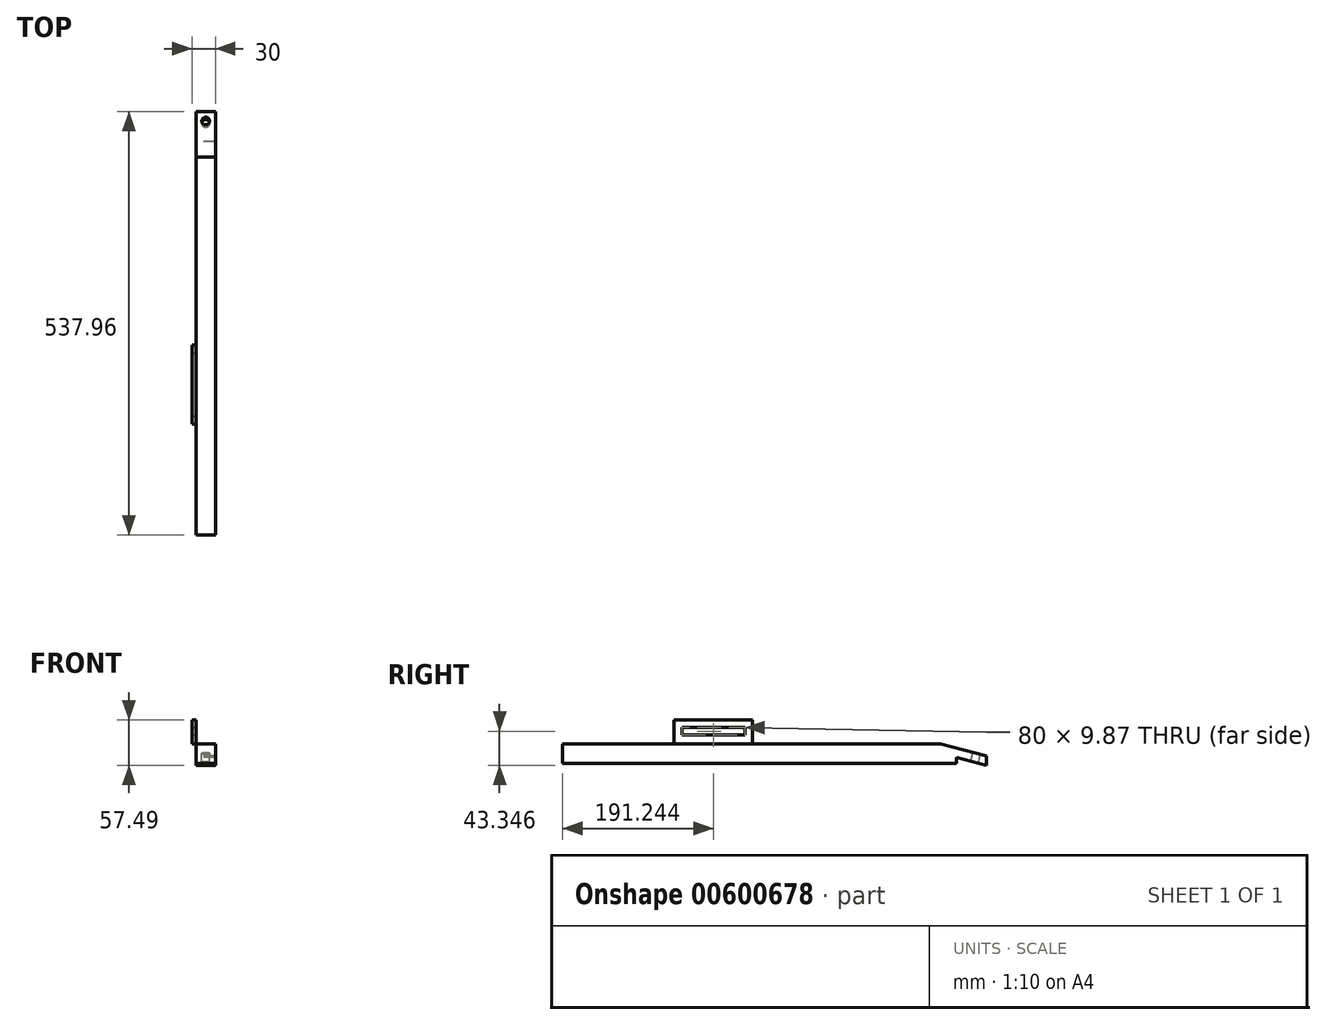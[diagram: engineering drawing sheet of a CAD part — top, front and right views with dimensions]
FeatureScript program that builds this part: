
annotation { "Feature Type Name" : "Feature", "Feature Type Description" : "" }
export const myFeature = defineFeature(function(context is Context, id is Id, definition is map)
    precondition{}
    {
        {
            var Q0;
            Q0=qCreatedBy(makeId("Right.planeOp"),FACE);
            var sketch = newSketch(context, id + "F0", { "sketchPlane" : qUnion([Q0])});
            skLineSegment(sketch, "E0.bottom", {"start": v(0, 0) * mm, "end": v(500, 0) * mm});
            skLineSegment(sketch, "E0.left", {"start": v(0, 0) * mm, "end": v(0, 25) * mm});
            skLineSegment(sketch, "E1", {"start": v(480, 25) * mm, "end": v(537.96, 9.47) * mm});
            skLineSegment(sketch, "E2", {"start": v(537.96, 9.47) * mm, "end": v(537.94, -2.49) * mm});
            skLineSegment(sketch, "E3", {"start": v(480, 25) * mm, "end": v(0, 25) * mm});
            skLineSegment(sketch, "E4", {"start": v(0, 25) * mm, "end": v(0, 0) * mm});
            skLineSegment(sketch, "E5", {"start": v(500, 0) * mm, "end": v(500, 7.68) * mm});
            skLineSegment(sketch, "E6", {"start": v(500, 7.68) * mm, "end": v(537.94, -2.49) * mm});
            skSolve(sketch);
        }
        {
            var Q0;
            Q0=makeQuery(id+"F0.imprint","IMPRINT",FACE,{"disambiguationData":[TD([[makeQuery(id+"F0.imprint","IMPRINT",EDGE,{"derivedFrom":sQuery(id+"F0.wireOp",EDGE,"E1")}),-1.0]])]});
            extrude(context, id + "F1", {"entities" : qUnion([Q0]), "depth" : 25 * mm, "offsetDistance" : 25 * mm});
        }
        {
            var Q0;
            Q0=makeQuery(id+"F1.opExtrude","SWEPT_FACE",FACE,{"disambiguationData":[OSD([sQuery(id+"F0.wireOp",EDGE,"E1")])]});
            var sketch = newSketch(context, id + "F2", { "sketchPlane" : qUnion([Q0])});
            skLineSegment(sketch, "E7.bottom", {"start": v(0, 517.17) * mm, "end": v(25, 517.17) * mm});
            skLineSegment(sketch, "E7.top", {"start": v(0, 457.17) * mm, "end": v(25, 457.17) * mm});
            skLineSegment(sketch, "E7.left", {"start": v(0, 517.17) * mm, "end": v(0, 457.17) * mm});
            skLineSegment(sketch, "E7.right", {"start": v(25, 517.17) * mm, "end": v(25, 457.17) * mm});
            skLineSegment(sketch, "E8", {"start": v(12.5, 517.17) * mm, "end": v(12.5, 504.83) * mm});
            skPoint(sketch, "E8.endSnap0", {"position": v(12.5, 517.17) * mm});
            skCircle(sketch, "E9", {"center": v(12.5, 504.83) * mm, "radius": 5 * mm});
            skSolve(sketch);
        }
        {
            var Q0;
            Q0=sQuery(id+"F2.wireOp",VERTEX,"E9.center");
            var Q1;
            Q1=makeQuery(id+"F1.opExtrude","SWEPT_BODY",BODY,{"disambiguationData":[OSD([sQuery(id+"F0.wireOp",EDGE,"E1"),sQuery(id+"F0.wireOp",EDGE,"E2"),sQuery(id+"F0.wireOp",EDGE,"E3"),sQuery(id+"F0.wireOp",EDGE,"E4"),sQuery(id+"F0.wireOp",EDGE,"E0.bottom"),sQuery(id+"F0.wireOp",EDGE,"E5"),sQuery(id+"F0.wireOp",EDGE,"E6")])]});
            hole(context, id + "F3", {"style" : HoleStyle.SIMPLE, "endStyle" : HoleEndStyle.THROUGH, "holeDiameter" : 10 * mm, "majorDiameter" : 5 * mm, "isTappedThrough" : true, "tappedDepth" : 12 * mm, "tapClearance" : 3, "locations" : qUnion([Q0]), "scope" : qUnion([Q1])});
        }
        {
            var Q0;
            Q0=makeQuery(id+"F0.imprint","IMPRINT",FACE,{"disambiguationData":[TD([[makeQuery(id+"F0.imprint","IMPRINT",EDGE,{"derivedFrom":sQuery(id+"F0.wireOp",EDGE,"E1")}),-1.0]])]});
            var sketch = newSketch(context, id + "F4", { "sketchPlane" : qUnion([Q0])});
            skLineSegment(sketch, "E10.bottom", {"start": v(0, 0) * mm, "end": v(482.49, 0) * mm});
            skLineSegment(sketch, "E10.top", {"start": v(0, 25.03) * mm, "end": v(482.49, 25.03) * mm});
            skLineSegment(sketch, "E10.left", {"start": v(0, 0) * mm, "end": v(0, 25.03) * mm});
            skLineSegment(sketch, "E10.right", {"start": v(482.49, 0) * mm, "end": v(482.49, 25.03) * mm});
            skLineSegment(sketch, "E11.bottom", {"start": v(241.24, 0) * mm, "end": v(141.24, 0) * mm});
            skLineSegment(sketch, "E11.top", {"start": v(241.24, 55) * mm, "end": v(141.24, 55) * mm});
            skLineSegment(sketch, "E11.left", {"start": v(241.24, 0) * mm, "end": v(241.24, 55) * mm});
            skLineSegment(sketch, "E11.right", {"start": v(141.24, 0) * mm, "end": v(141.24, 55) * mm});
            skLineSegment(sketch, "E12.bottom", {"start": v(231.24, 35.92) * mm, "end": v(151.24, 35.92) * mm});
            skLineSegment(sketch, "E12.top", {"start": v(231.24, 45.79) * mm, "end": v(151.24, 45.79) * mm});
            skLineSegment(sketch, "E12.left", {"start": v(231.24, 35.92) * mm, "end": v(231.24, 45.79) * mm});
            skLineSegment(sketch, "E12.right", {"start": v(151.24, 35.92) * mm, "end": v(151.24, 45.79) * mm});
            skSolve(sketch);
        }
        {
            var Q0;
            {var subQ1=sQuery(id+"F4.wireOp",EDGE,"E11.top");Q0=makeQuery(id+"F4.imprint","IMPRINT",FACE,{"disambiguationData":[TD([[makeQuery(id+"F4.imprint","IMPRINT",EDGE,{"derivedFrom":subQ1}),1.0]])]});}
            var Q1;
            {var subQ0=sQuery(id+"F4.wireOp",EDGE,"E11.bottom");Q1=makeQuery(id+"F4.imprint","IMPRINT",FACE,{"disambiguationData":[TD([[makeQuery(id+"F4.imprint","IMPRINT",EDGE,{"derivedFrom":subQ0}),1.0]])]});}
            extrude(context, id + "F5", {"entities" : qUnion([Q0, Q1]), "operationType" : NewBodyOperationType.ADD, "oppositeDirection" : true, "depth" : 5 * mm, "offsetDistance" : 25 * mm});
        }
    });
